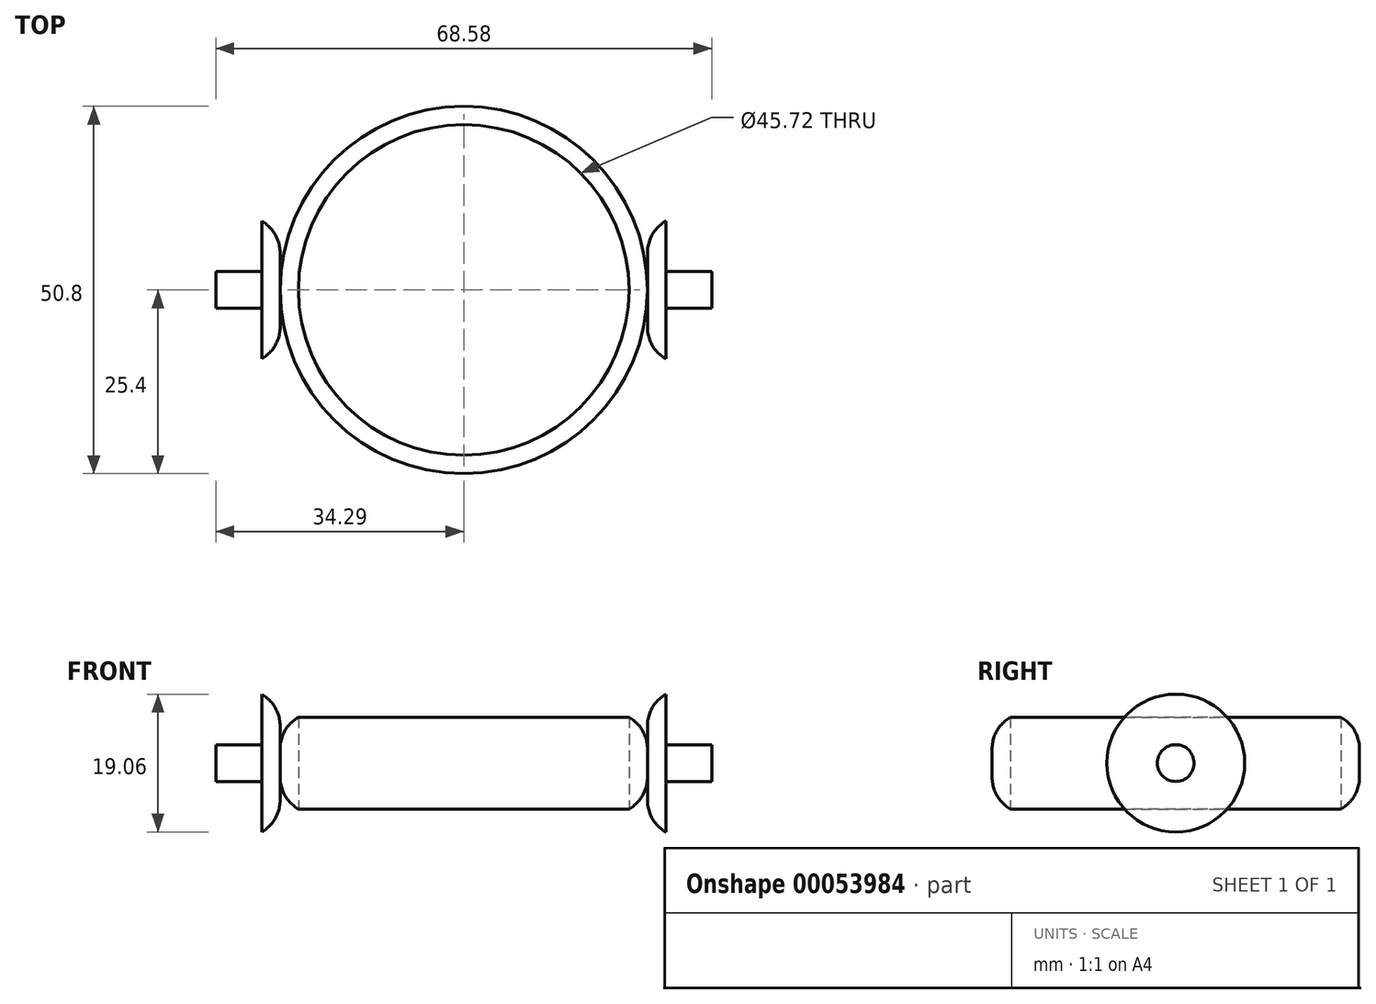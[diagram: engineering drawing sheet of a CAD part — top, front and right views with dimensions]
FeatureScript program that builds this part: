
annotation { "Feature Type Name" : "Feature", "Feature Type Description" : "" }
export const myFeature = defineFeature(function(context is Context, id is Id, definition is map)
    precondition{}
    {
        {
            var Q0;
            Q0=qCreatedBy(makeId("Top.planeOp"),FACE);
            var sketch = newSketch(context, id + "F0", { "sketchPlane" : qUnion([Q0])});
            skCircle(sketch, "E0", {"center": v(0, 0) * mm, "radius": 25.4 * mm});
            skCircle(sketch, "E1", {"center": v(0, 0) * mm, "radius": 22.86 * mm});
            skSolve(sketch);
        }
        {
            var Q0;
            Q0=makeQuery(id+"F0.imprint","IMPRINT",FACE,{"disambiguationData":[TD([[makeQuery(id+"F0.imprint","IMPRINT",EDGE,{"derivedFrom":sQuery(id+"F0.wireOp",EDGE,"E0")}),1.0]])]});
            extrude(context, id + "F1", {"entities" : qUnion([Q0]), "endBound" : BoundingType.SYMMETRIC, "depth" : 12.7 * mm});
        }
        {
            var Q0;
            Q0=qCreatedBy(makeId("Right.planeOp"),FACE);
            var sketch = newSketch(context, id + "F2", { "sketchPlane" : qUnion([Q0])});
            skCircle(sketch, "E2", {"center": v(0, 0) * mm, "radius": 9.53 * mm});
            skSolve(sketch);
        }
        {
            var Q0;
            Q0 = qSketchRegion(id + "F2", true);
            extrude(context, id + "F3", {"entities" : qUnion([Q0]), "operationType" : NewBodyOperationType.ADD, "depth" : 2.54 * mm});
        }
        {
            var Q0;
            Q0=makeQuery(id+"F3.opExtrude","SWEPT_BODY",BODY,{"disambiguationData":[OSD([sQuery(id+"F2.wireOp",EDGE,"E2")])]});
            var Q1;
            Q1=makeQuery(id+"F3.opExtrude","CAP_EDGE",EDGE,{"disambiguationData":[OSD([sQuery(id+"F2.wireOp",EDGE,"E2")])],"isStart":true});
            var Q2;
            Q2=makeQuery(id+"F3.opExtrude","CAP_EDGE",EDGE,{"disambiguationData":[OSD([sQuery(id+"F2.wireOp",EDGE,"E2")])],"isStart":false});
            var Q3;
            Q3=qCreatedBy(makeId("Right.planeOp"),FACE);
            transform(context, id + "F4", {"entities" : qUnion([Q0]), "transformType" : TransformType.TRANSLATION_DISTANCE, "transformDirection" : qUnion([Q3]), "distance" : 25.4 * mm, "makeCopy" : false});
        }
        {
            var Q0;
            Q0=makeQuery(id+"F1.opExtrude","CAP_EDGE",EDGE,{"disambiguationData":[OSD([sQuery(id+"F0.wireOp",EDGE,"E0")])],"isStart":false});
            var Q1;
            Q1=makeQuery(id+"F3.opExtrude","CAP_FACE",FACE,{"disambiguationData":[OSD([sQuery(id+"F2.wireOp",EDGE,"E2")])],"isStart":true});
            fillet(context, id + "F5", {"entities" : qUnion([Q0, Q1]), "radius" : 5.08 * mm, "tangentPropagation" : true, "allowEdgeOverflow" : false});
        }
        {
            var Q0;
            Q0=makeQuery(id+"F1.opExtrude","CAP_EDGE",EDGE,{"disambiguationData":[OSD([sQuery(id+"F0.wireOp",EDGE,"E0")])],"isStart":true});
            var Q1;
            {var subQ0=sQuery(id+"F2.wireOp",EDGE,"E2");Q1=makeQuery(id+"F5.opFillet","BLEND_EDGE",EDGE,{"blendedFrom":[makeQuery(id+"F3.opExtrude","CAP_EDGE",EDGE,{"disambiguationData":[OSD([subQ0])],"isStart":true}),makeQuery(id+"F3.opExtrude","CAP_FACE",FACE,{"disambiguationData":[OSD([subQ0])],"isStart":true})],"blendedInto":[makeQuery(id+"F3.opExtrude","CAP_FACE",FACE,{"disambiguationData":[OSD([subQ0])],"isStart":true})]});}
            fillet(context, id + "F6", {"entities" : qUnion([Q0, Q1]), "radius" : 5.08 * mm, "tangentPropagation" : true, "allowEdgeOverflow" : false});
        }
        {
            var Q0;
            Q0=makeQuery(id+"F3.opExtrude","CAP_FACE",FACE,{"disambiguationData":[OSD([sQuery(id+"F2.wireOp",EDGE,"E2")])],"isStart":false});
            var sketch = newSketch(context, id + "F7", { "sketchPlane" : qUnion([Q0])});
            skCircle(sketch, "E3", {"center": v(0, 0) * mm, "radius": 2.54 * mm});
            skSolve(sketch);
        }
        {
            var Q0;
            Q0 = qSketchRegion(id + "F7", true);
            extrude(context, id + "F8", {"entities" : qUnion([Q0]), "operationType" : NewBodyOperationType.ADD, "depth" : 6.35 * mm});
        }
        {
            var Q0;
            Q0=makeQuery(id+"F3.opExtrude","SWEPT_BODY",BODY,{"disambiguationData":[OSD([sQuery(id+"F2.wireOp",EDGE,"E2")])]});
            var Q1;
            Q1=qCreatedBy(makeId("Right.planeOp"),FACE);
            mirror(context, id + "F9", {"operationType" : NewBodyOperationType.ADD, "entities" : qUnion([Q0]), "mirrorPlane" : qUnion([Q1])});
        }
    });
